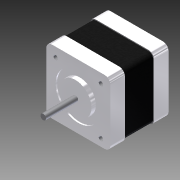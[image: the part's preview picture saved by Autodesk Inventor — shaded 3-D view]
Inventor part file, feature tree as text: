
AUTODESK INVENTOR PART (.ipt)
format: ipt  version: 2012 SP1 (Build 160190100, 190)  size: 195,584 bytes
history: native  units: in
note: dims shown in document units (in); Inventor stores cm internally (conversion verified against a paired STEP export)
features: extrude x6, sketch x6, fillet x1
ambient origin geometry x8: Origin, YZ Plane, XZ Plane, XY Plane, X Axis, Y Axis, Z Axis, Center Point
bodies: Solid1 (feature_tree)
feature tree (13):
  extrude  "Extrusion1"  Depth=1.6654in
  fillet  "Fillet1"  Radius=0.8661in
  extrude  "Extrusion2"  Depth=0.1181in
  extrude  "Extrusion3"  Depth=0.1181in
  extrude  "Extrusion4"  Depth=1.5748in TaperAngle=0.0deg
  extrude  "Extrusion5"  Depth=0.0787in TaperAngle=0.0deg
  extrude  "Extrusion6"  Depth=0.8661in TaperAngle=0.0deg
  sketch  "Sketch1"  dims[d0=1.6654in d1=1.6654in d2=0.8661in]
  sketch  "Sketch2"  dims[d3=1.2205in d4=0.1181in]
  sketch  "Sketch3"  dims[d5=0.1181in d6=0.1181in]
  sketch  "Sketch4"  dims[d7=0.1181in d8=1.5748in d9=0.0in]
  sketch  "Sketch5"  dims[d10=0.125in d11=0.0787in d12=0.0in]
  sketch  "Sketch6"  dims[d13=0.0394in d14=0.0in d15=0.8661in d16=0.0in d17=0.3937in d18=0.0in d19=0.3937in d20=0.0in]
